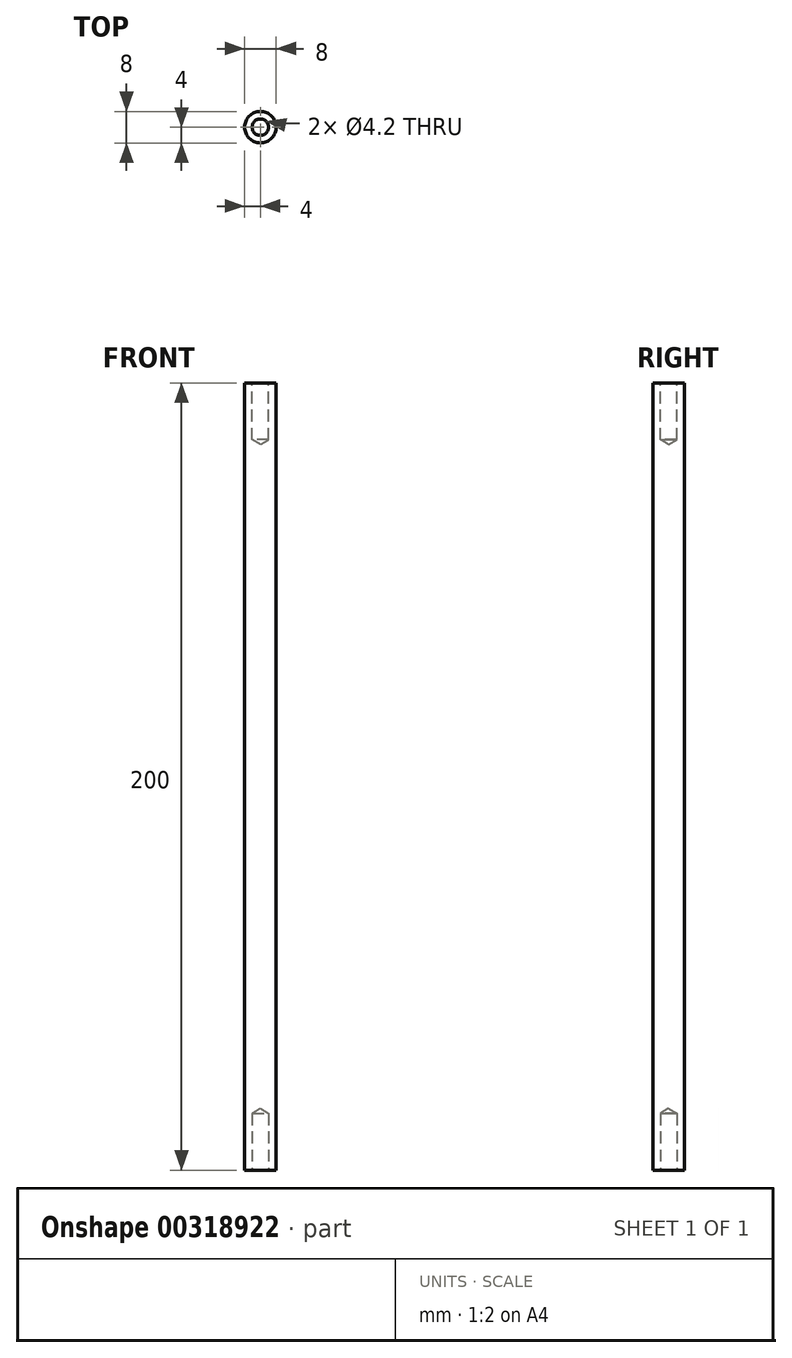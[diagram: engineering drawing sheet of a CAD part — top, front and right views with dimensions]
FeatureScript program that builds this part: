
annotation { "Feature Type Name" : "Feature", "Feature Type Description" : "" }
export const myFeature = defineFeature(function(context is Context, id is Id, definition is map)
    precondition{}
    {
        {
            var Q0;
            Q0=qCreatedBy(makeId("Top.planeOp"),FACE);
            var sketch = newSketch(context, id + "F0", { "sketchPlane" : qUnion([Q0])});
            skCircle(sketch, "E0", {"center": v(0, 0) * mm, "radius": 4 * mm});
            skSolve(sketch);
        }
        {
            var Q0;
            Q0=makeQuery(id+"F0.imprint","IMPRINT",FACE,{"disambiguationData":[TD([[makeQuery(id+"F0.imprint","IMPRINT",EDGE,{"derivedFrom":sQuery(id+"F0.wireOp",EDGE,"E0")}),1.0]])]});
            extrude(context, id + "F1", {"entities" : qUnion([Q0]), "depth" : 200 * mm});
        }
        {
            var Q0;
            Q0=makeQuery(id+"F1.opExtrude","CAP_FACE",FACE,{"disambiguationData":[OSD([sQuery(id+"F0.wireOp",EDGE,"E0")])],"isStart":false});
            var sketch = newSketch(context, id + "F2", { "sketchPlane" : qUnion([Q0])});
            skCircle(sketch, "E1", {"center": v(0, 0) * mm, "radius": 1.64 * mm});
            skSolve(sketch);
        }
        {
            var Q0;
            Q0=sQuery(id+"F2.wireOp",VERTEX,"E1.center");
            var Q1;
            Q1=makeQuery(id+"F1.opExtrude","SWEPT_BODY",BODY,{"disambiguationData":[OSD([sQuery(id+"F0.wireOp",EDGE,"E0")])]});
            hole(context, id + "F3", {"style" : HoleStyle.SIMPLE, "endStyle" : HoleEndStyle.BLIND, "standardTappedOrClearance" : lookupTablePath({ "standard" : "ISO", "engagement" : "75%", "pitch" : "0.8 mm", "size" : "M5", "type" : "Tapped" }), "standardBlindInLast" : lookupTablePath({ "standard" : "ISO", "engagement" : "75%", "pitch" : "0.8 mm", "size" : "M5", "type" : "Tapped" }), "holeDiameter" : 4.2 * mm, "showTappedDepth" : true, "holeDepth" : 14.4 * mm, "tappedDepth" : 12 * mm, "tapClearance" : 3, "startFromSketch" : true, "locations" : qUnion([Q0]), "scope" : qUnion([Q1]), "majorDiameter" : 5 * mm});
        }
        {
            var Q0;
            Q0=qCreatedBy(makeId("Top.planeOp"),FACE);
            var sketch = newSketch(context, id + "F4", { "sketchPlane" : qUnion([Q0])});
            skCircle(sketch, "E2", {"center": v(0, 0) * mm, "radius": 1.93 * mm});
            skSolve(sketch);
        }
        {
            var Q0;
            Q0=sQuery(id+"F4.wireOp",VERTEX,"E2.center");
            var Q1;
            Q1=makeQuery(id+"F1.opExtrude","SWEPT_BODY",BODY,{"disambiguationData":[OSD([sQuery(id+"F0.wireOp",EDGE,"E0")])]});
            hole(context, id + "F5", {"style" : HoleStyle.SIMPLE, "endStyle" : HoleEndStyle.BLIND, "oppositeDirection" : true, "standardTappedOrClearance" : lookupTablePath({ "standard" : "ISO", "engagement" : "75%", "pitch" : "0.8 mm", "size" : "M5", "type" : "Tapped" }), "standardBlindInLast" : lookupTablePath({ "standard" : "ISO", "engagement" : "75%", "pitch" : "0.8 mm", "size" : "M5", "type" : "Tapped" }), "holeDiameter" : 4.2 * mm, "showTappedDepth" : true, "holeDepth" : 14.4 * mm, "tappedDepth" : 12 * mm, "tapClearance" : 3, "startFromSketch" : true, "locations" : qUnion([Q0]), "scope" : qUnion([Q1]), "majorDiameter" : 5 * mm});
        }
    });
